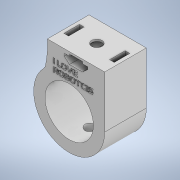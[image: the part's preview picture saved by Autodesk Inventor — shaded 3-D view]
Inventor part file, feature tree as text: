
AUTODESK INVENTOR PART (.ipt)
format: ipt  version: 2020 (Build 240168000, 168)  size: 729,600 bytes
history: native  units: in
note: dims shown in document units (in); Inventor stores cm internally (conversion verified against a paired STEP export)
features: extrude x5, sketch x4, plane x2, fillet x1, emboss x1
ambient origin geometry x8: Origin, YZ Plane, XZ Plane, XY Plane, X Axis, Y Axis, Z Axis, Center Point
bodies: Body1 (feature_tree)
feature tree (13):
  sketch  "Sketch5"  dims[d0=1.1in d1=1.0in]
  plane  "Work Plane4"
  extrude  "Extrusion7"  Depth=1.0in
  extrude  "Extrusion8"  Depth=0.175in
  extrude  "Extrusion9"  Depth=0.1in
  fillet  "Fillet1"  Radius=0.2in
  extrude  "Extrusion10"  Depth=0.8in TaperAngle=0.0deg
  plane  "Work Plane5"
  extrude  "Extrusion11"  Depth=0.6in TaperAngle=0.0deg
  emboss  "Emboss1"
  sketch  "Sketch10"  dims[d2=0.93in d5=0.175in]
  sketch  "Sketch11"  dims[d6=0.45in d7=0.1in d19=0.2in]
  sketch  "Sketch12"  dims[d25=0.8in d26=0.0in d27=0.8in d28=0.0in d29=0.6in d30=0.0in d31=0.125in d32=0.09in d33=0.3in d34=0.1in d35=0.0in d36=0.2in d37=0.6in d38=0.0in d39=0.1in d40=0.0in]
